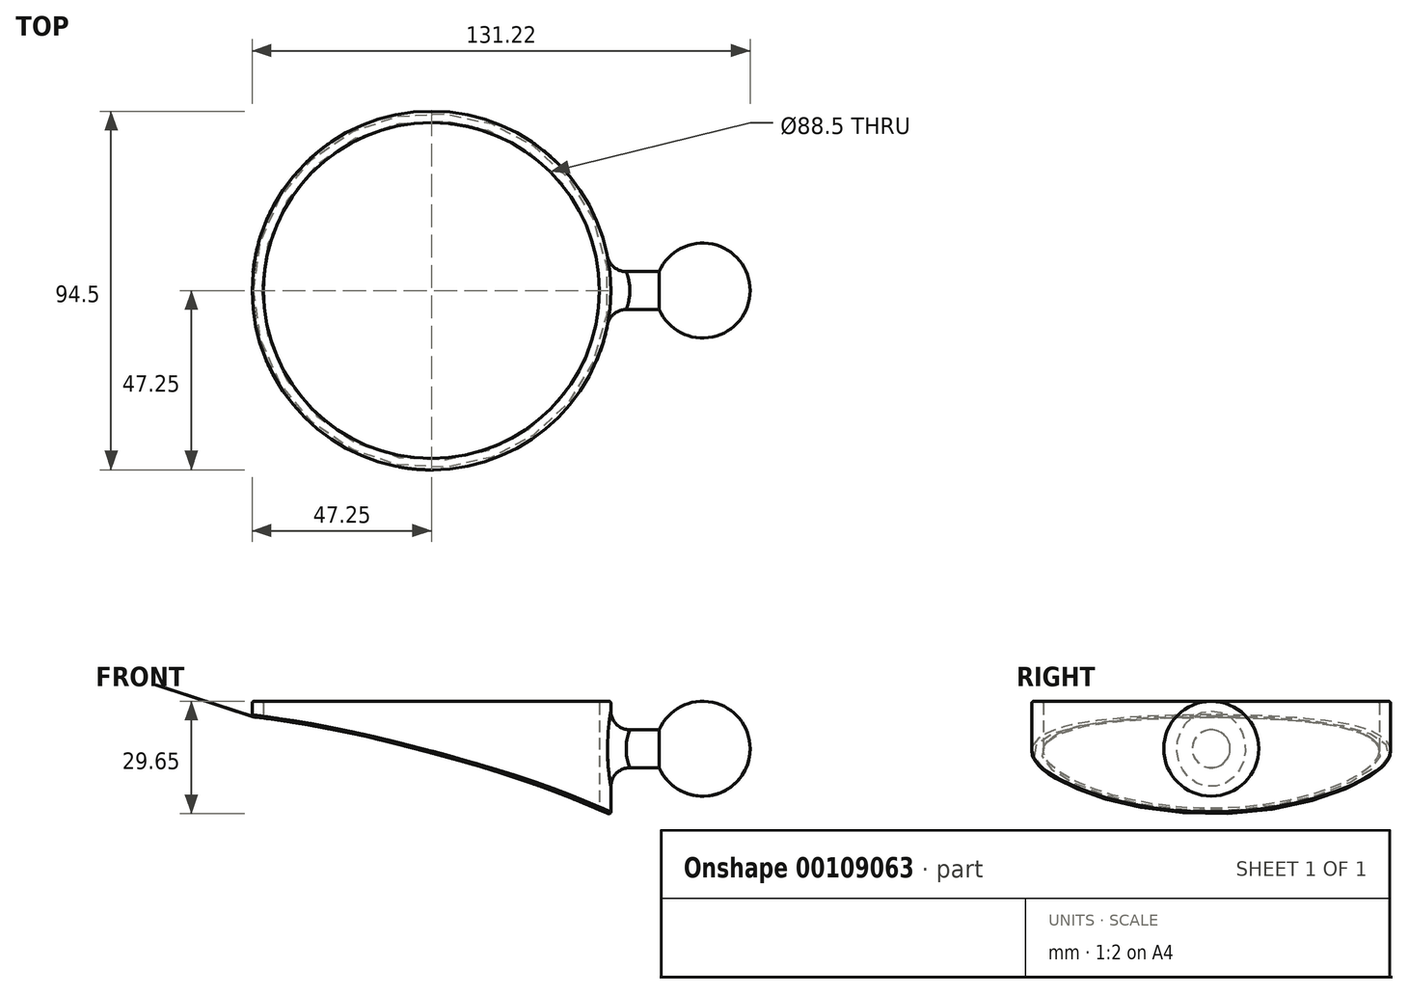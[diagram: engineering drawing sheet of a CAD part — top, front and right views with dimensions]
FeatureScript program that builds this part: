
annotation { "Feature Type Name" : "Feature", "Feature Type Description" : "" }
export const myFeature = defineFeature(function(context is Context, id is Id, definition is map)
    precondition{}
    {
        {
            var Q0;
            Q0=qCreatedBy(makeId("Top.planeOp"),FACE);
            var sketch = newSketch(context, id + "F0", { "sketchPlane" : qUnion([Q0])});
            skCircle(sketch, "E0", {"center": v(0, 0) * mm, "radius": 44.25 * mm});
            skCircle(sketch, "E1.0", {"center": v(0, 0) * mm, "radius": 47.25 * mm});
            skSolve(sketch);
        }
        {
            var Q0;
            Q0=makeQuery(id+"F0.imprint","IMPRINT",FACE,{"disambiguationData":[TD([[makeQuery(id+"F0.imprint","IMPRINT",EDGE,{"derivedFrom":sQuery(id+"F0.wireOp",EDGE,"E0")}),-1.0]])]});
            extrude(context, id + "F1", {"entities" : qUnion([Q0]), "depth" : 30 * mm});
        }
        {
            var Q0;
            Q0=qCreatedBy(makeId("Front.planeOp"),FACE);
            var sketch = newSketch(context, id + "F2", { "sketchPlane" : qUnion([Q0])});
            skFitSpline(sketch, "E2", {"points": [v(-47.4, 26) * mm, v(0, 16.4) * mm, v(47.43, 0) * mm], "startDerivative": vector(116.92, -14.47) * mm, "endDerivative": vector(107.2, -48.58) * mm});
            skLineSegment(sketch, "E3", {"start": v(47.43, 0) * mm, "end": v(-47.28, 0) * mm});
            skLineSegment(sketch, "E4", {"start": v(-47.28, 0) * mm, "end": v(-47.4, 26) * mm});
            skSolve(sketch);
        }
        {
            var Q0;
            Q0 = qSketchRegion(id + "F2", true);
            extrude(context, id + "F3", {"entities" : qUnion([Q0]), "operationType" : NewBodyOperationType.REMOVE, "oppositeDirection" : true, "depth" : 95 * mm, "symmetric" : true});
        }
        {
            var Q0;
            Q0=qCreatedBy(makeId("Front.planeOp"),FACE);
            var sketch = newSketch(context, id + "F4", { "sketchPlane" : qUnion([Q0])});
            skLineSegment(sketch, "E5", {"start": v(46.97, 17.5) * mm, "end": v(83.97, 17.5) * mm});
            skArc(sketch, "E6", {"start": v(83.97, 17.5) * mm, "mid": v(74.02, 29.74) * mm, "end": v(60.01, 22.5) * mm});
            skLineSegment(sketch, "E7", {"start": v(46.34, 22.5) * mm, "end": v(60.01, 22.5) * mm});
            skLineSegment(sketch, "E8", {"start": v(46.34, 22.5) * mm, "end": v(46.97, 17.5) * mm});
            skSolve(sketch);
        }
        {
            var Q0;
            Q0 = qSketchRegion(id + "F4", true);
            var Q1;
            Q1=sQuery(id+"F4.wireOp",EDGE,"E5");
            revolve(context, id + "F5", {"operationType" : NewBodyOperationType.ADD, "entities" : qUnion([Q0]), "axis" : qUnion([Q1]), "revolveType" : RevolveType.FULL});
        }
        {
            var Q0;
            Q0=makeQuery(id+"F5.boolean.opBoolean","INTERSECT",EDGE,{"derivedFrom":[makeQuery(id+"F1.opExtrude","SWEPT_FACE",FACE,{"disambiguationData":[OSD([sQuery(id+"F0.wireOp",EDGE,"E1.0")])]}),makeQuery(id+"F5.opRevolve","SWEPT_FACE",FACE,{"disambiguationData":[OSD([sQuery(id+"F4.wireOp",EDGE,"E7")])]})]});
            fillet(context, id + "F6", {"entities" : qUnion([Q0]), "radius" : 5 * mm, "tangentPropagation" : true, "allowEdgeOverflow" : false});
        }
        {
            var Q0;
            Q0=makeQuery(id+"F1.opExtrude","CAP_EDGE",EDGE,{"disambiguationData":[OSD([sQuery(id+"F0.wireOp",EDGE,"E0")])],"isStart":false});
            var Q1;
            Q1=makeQuery(id+"F1.opExtrude","CAP_EDGE",EDGE,{"disambiguationData":[OSD([sQuery(id+"F0.wireOp",EDGE,"E1.0")])],"isStart":false});
            var Q2;
            Q2=makeQuery(id+"F3.boolean.opBoolean","INTERSECT",EDGE,{"derivedFrom":[makeQuery(id+"F1.opExtrude","SWEPT_FACE",FACE,{"disambiguationData":[OSD([sQuery(id+"F0.wireOp",EDGE,"E0")])]}),makeQuery(id+"F3.opExtrude","SWEPT_FACE",FACE,{"disambiguationData":[OSD([sQuery(id+"F2.wireOp",EDGE,"E2")])]})]});
            var Q3;
            Q3=makeQuery(id+"F3.boolean.opBoolean","INTERSECT",EDGE,{"derivedFrom":[makeQuery(id+"F1.opExtrude","SWEPT_FACE",FACE,{"disambiguationData":[OSD([sQuery(id+"F0.wireOp",EDGE,"E1.0")])]}),makeQuery(id+"F3.opExtrude","SWEPT_FACE",FACE,{"disambiguationData":[OSD([sQuery(id+"F2.wireOp",EDGE,"E2")])]})]});
            fillet(context, id + "F7", {"entities" : qUnion([Q0, Q1, Q2, Q3]), "radius" : 0.5 * mm, "tangentPropagation" : true, "allowEdgeOverflow" : false});
        }
    });
